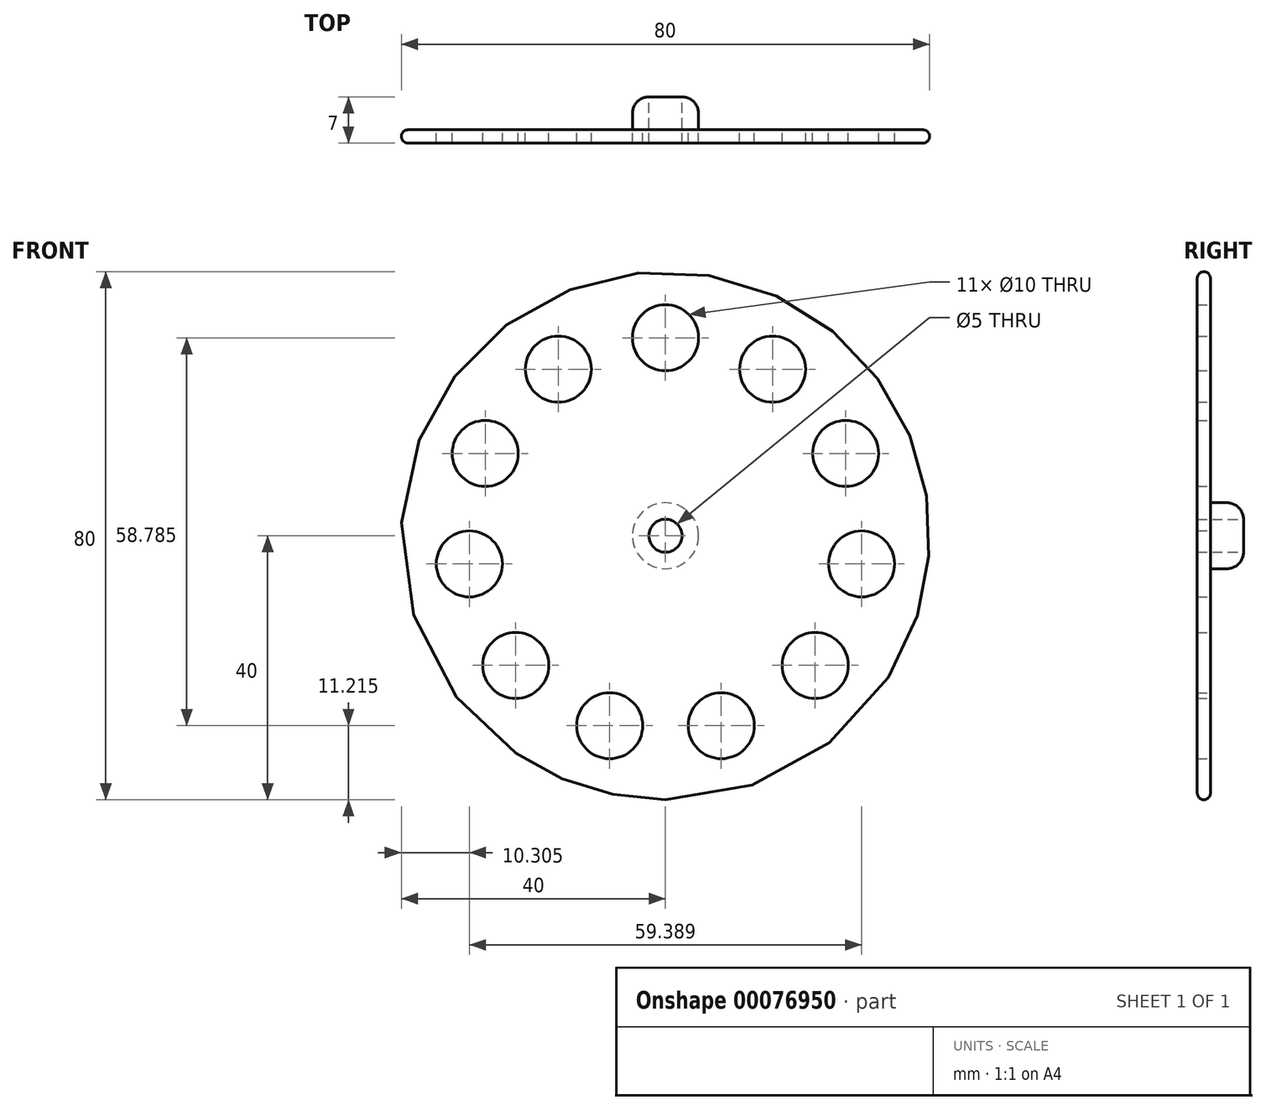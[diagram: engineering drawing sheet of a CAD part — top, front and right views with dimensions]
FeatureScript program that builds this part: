
annotation { "Feature Type Name" : "Feature", "Feature Type Description" : "" }
export const myFeature = defineFeature(function(context is Context, id is Id, definition is map)
    precondition{}
    {
        {
            var Q0;
            Q0=qCreatedBy(makeId("Front.planeOp"),FACE);
            var sketch = newSketch(context, id + "F0", { "sketchPlane" : qUnion([Q0])});
            skCircle(sketch, "E0", {"center": v(0, 0) * mm, "radius": 40 * mm});
            skCircle(sketch, "E1", {"center": v(0, 30) * mm, "radius": 5 * mm});
            skCircle(sketch, "E2", {"center": v(0, 0) * mm, "radius": 5 * mm, "construction": true});
            skCircle(sketch, "E3", {"center": v(0, 0) * mm, "radius": 2.5 * mm});
            skCircle(sketch, "E4", {"center": v(0, 0) * mm, "radius": 7.42 * mm, "construction": true});
            skCircle(sketch, "E5.1.0", {"center": v(-16.22, 25.24) * mm, "radius": 5 * mm});
            skCircle(sketch, "E5.2.0", {"center": v(-27.29, 12.46) * mm, "radius": 5 * mm});
            skLineSegment(sketch, "E5.anchor1", {"start": v(0, 0) * mm, "end": v(0, 30) * mm, "construction": true});
            skLineSegment(sketch, "E5.anchor2", {"start": v(0, 0) * mm, "end": v(16.22, 25.24) * mm, "construction": true});
            skCircle(sketch, "E6.1.3.0", {"center": v(-29.7, -4.27) * mm, "radius": 5 * mm});
            skCircle(sketch, "E6.1.4.0", {"center": v(-22.67, -19.65) * mm, "radius": 5 * mm});
            skCircle(sketch, "E6.1.5.0", {"center": v(-8.45, -28.78) * mm, "radius": 5 * mm});
            skCircle(sketch, "E6.1.6.0", {"center": v(8.45, -28.78) * mm, "radius": 5 * mm});
            skCircle(sketch, "E6.1.7.0", {"center": v(22.67, -19.65) * mm, "radius": 5 * mm});
            skCircle(sketch, "E6.1.8.0", {"center": v(29.7, -4.27) * mm, "radius": 5 * mm});
            skCircle(sketch, "E6.1.9.0", {"center": v(27.29, 12.46) * mm, "radius": 5 * mm});
            skCircle(sketch, "E6.1.10.0", {"center": v(16.22, 25.24) * mm, "radius": 5 * mm});
            skSolve(sketch);
        }
        {
            var Q0;
            Q0=qSketchRegion(id+"F0",true);
            extrude(context, id + "F1", {"entities" : qUnion([Q0]), "depth" : 2 * mm});
        }
        {
            var Q0;
            Q0=qCreatedBy(makeId("Front.planeOp"),FACE);
            var sketch = newSketch(context, id + "F2", { "sketchPlane" : qUnion([Q0])});
            skCircle(sketch, "E7.0", {"center": v(0, 0) * mm, "radius": 5 * mm});
            skCircle(sketch, "E8.0", {"center": v(0, 0) * mm, "radius": 2.5 * mm});
            skSolve(sketch);
        }
        {
            var Q0;
            Q0=qSketchRegion(id+"F2",true);
            extrude(context, id + "F3", {"entities" : qUnion([Q0]), "operationType" : NewBodyOperationType.ADD, "oppositeDirection" : true, "depth" : 5 * mm});
        }
        {
            var Q0;
            Q0=makeQuery(id+"F3.opExtrude","CAP_EDGE",EDGE,{"disambiguationData":[OSD([sQuery(id+"F2.wireOp",EDGE,"E7.0")])],"isStart":true});
            var Q1;
            Q1=makeQuery(id+"F3.opExtrude","CAP_EDGE",EDGE,{"disambiguationData":[OSD([sQuery(id+"F2.wireOp",EDGE,"E7.0")])],"isStart":false});
            fillet(context, id + "F4", {"entities" : qUnion([Q0, Q1]), "radius" : 2.5 * mm, "tangentPropagation" : true, "allowEdgeOverflow" : false});
        }
        {
            var Q0;
            Q0=makeQuery(id+"F1.opExtrude","SWEPT_FACE",FACE,{"disambiguationData":[OSD([sQuery(id+"F0.wireOp",EDGE,"E0")])]});
            fillet(context, id + "F5", {"entities" : qUnion([Q0]), "radius" : 1 * mm, "tangentPropagation" : true, "allowEdgeOverflow" : false});
        }
    });
